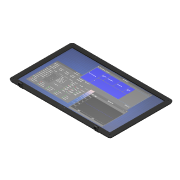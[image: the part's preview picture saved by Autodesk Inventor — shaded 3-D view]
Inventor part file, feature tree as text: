
AUTODESK INVENTOR PART (.ipt)
format: ipt  version: 2022 (Build 260153000, 153)  size: 1,221,632 bytes
history: native  units: mm
features: fillet x14, sketch x10, extrude x9, mirror x2, other x2, plane x1, revolve x1
ambient origin geometry x8: Origin, YZ Plane, XZ Plane, XY Plane, X Axis, Y Axis, Z Axis, Center Point
bodies: Solid1 (feature_tree), Solid2 (feature_tree)
feature tree (39):
  extrude  "Extrusion1"  Depth=220.0mm
  extrude  "Extrusion2"  Depth=10.0mm
  plane  "Work Plane1"
  extrude  "Extrusion3"  Depth=3.0mm TaperAngle=0.0deg
  fillet  "Fillet1"  [1 undecoded]
  fillet  "Fillet2"  Radius=3.0mm
  mirror  "Mirror2"
  extrude  "Extrusion4"  Depth=10.0mm
  fillet  "Fillet3"  Radius=10.0mm
  extrude  "Extrusion5"  Depth=2.0mm
  revolve  "Revolution1"  [1 undecoded]
  fillet  "Fillet4"  Radius=5.0mm
  extrude  "Extrusion6"  TaperAngle=90.0deg  [1 undecoded]
  fillet  "Fillet5"  Radius=0.1mm
  fillet  "Fillet6"  Radius=2.0mm
  mirror  "Mirror3"
  fillet  "Fillet7"  Radius=1.0mm
  fillet  "Fillet8"  Radius=1.0mm
  fillet  "Fillet9"  Radius=1.0mm
  fillet  "Fillet10"  Radius=0.1mm
  extrude  "Extrusion7"  Depth=0.1mm
  fillet  "Fillet11"  Radius=1.0mm
  fillet  "Fillet12"  Radius=1.0mm
  fillet  "Fillet13"  Radius=0.1mm
  fillet  "Fillet14"  Radius=0.1mm
  extrude  "Extrusion8"  Depth=0.1mm TaperAngle=0.0deg
  extrude  "Extrusion9"  [1 undecoded]
  other  "Decal1"
  sketch  "Sketch1"  dims[d0=350.0mm d1=220.0mm]
  sketch  "Sketch2"  dims[d2=10.0mm d3=0.0mm d4=320.0mm]
  sketch  "Sketch4"  dims[d5=190.0mm d6=3.0mm d7=0.0mm d8=-40.0mm d9=3.0mm]
  sketch  "Sketch5"  dims[d10=10.0mm d11=0.0mm d12=10.0mm d13=10.0mm]
  sketch  "Sketch6"  dims[d14=1.0mm d15=0.0mm d16=2.0mm]
  sketch  "Sketch7"  dims[d17=3.0mm d18=0.1mm d19=0.0mm d20=5.0mm]
  sketch  "Sketch8"  dims[d21=5.0mm d22=90.0deg d23=0.1mm d24=2.0mm d25=0.0mm d26=1.0mm d27=1.0mm d28=1.0mm d29=0.1mm]
  sketch  "Sketch9"  dims[d30=0.1mm d31=0.1mm d33=1.0mm d34=0.0mm d35=1.0mm d36=0.1mm d37=0.1mm]
  sketch  "Sketch10"  dims[d38=0.1mm d39=0.1mm d40=0.0mm]
  sketch  "Sketch12"  dims[d41=0.1mm d42=0.0mm]
  other  "Image3"
note: 4 required parameter values undecoded (feature->parameter linkage not recoverable at this tier; creation-order binding heuristic only, values carry confidence <= 0.55)